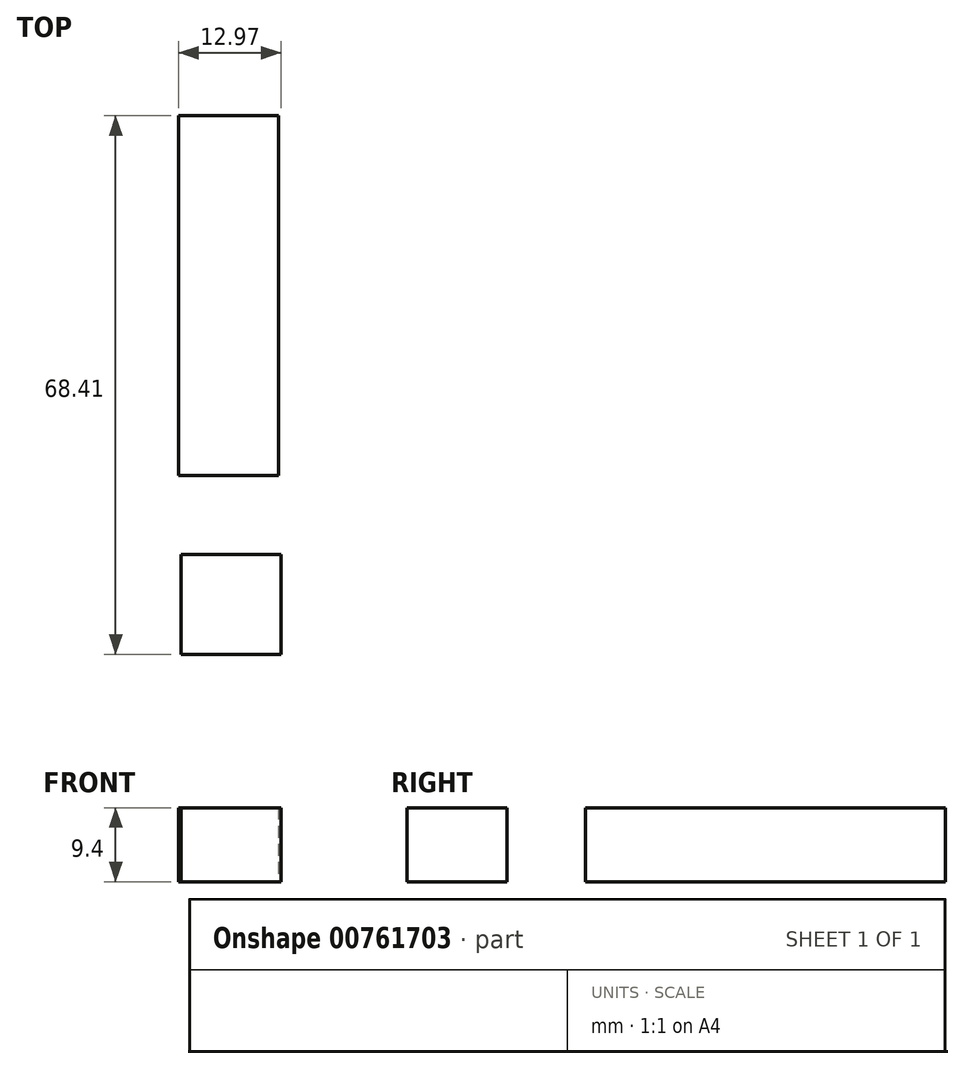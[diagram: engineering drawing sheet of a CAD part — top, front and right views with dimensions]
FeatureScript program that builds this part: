
annotation { "Feature Type Name" : "Feature", "Feature Type Description" : "" }
export const myFeature = defineFeature(function(context is Context, id is Id, definition is map)
    precondition{}
    {
        {
            var Q0;
            Q0=qCreatedBy(makeId("Top.planeOp"),FACE);
            var sketch = newSketch(context, id + "F0", { "sketchPlane" : qUnion([Q0])});
            skLineSegment(sketch, "E0.bottom", {"start": v(-7.92, -9.99) * mm, "end": v(4.78, -9.99) * mm});
            skLineSegment(sketch, "E0.top", {"start": v(-7.92, -22.69) * mm, "end": v(4.78, -22.69) * mm});
            skLineSegment(sketch, "E0.left", {"start": v(-7.92, -9.99) * mm, "end": v(-7.92, -22.69) * mm});
            skLineSegment(sketch, "E0.right", {"start": v(4.78, -9.99) * mm, "end": v(4.78, -22.69) * mm});
            skLineSegment(sketch, "E1.bottom", {"start": v(-8.19, 0) * mm, "end": v(4.51, 0) * mm});
            skLineSegment(sketch, "E1.top", {"start": v(-8.19, 45.72) * mm, "end": v(4.51, 45.72) * mm});
            skLineSegment(sketch, "E1.left", {"start": v(-8.19, 0) * mm, "end": v(-8.19, 45.72) * mm});
            skLineSegment(sketch, "E1.right", {"start": v(4.51, 0) * mm, "end": v(4.51, 45.72) * mm});
            skSolve(sketch);
        }
        {
            var Q0;
            Q0 = qSketchRegion(id + "F0", true);
            extrude(context, id + "F1", {"entities" : qUnion([Q0]), "depth" : 9.4 * mm, "offsetDistance" : 25.4 * mm});
        }
    });
